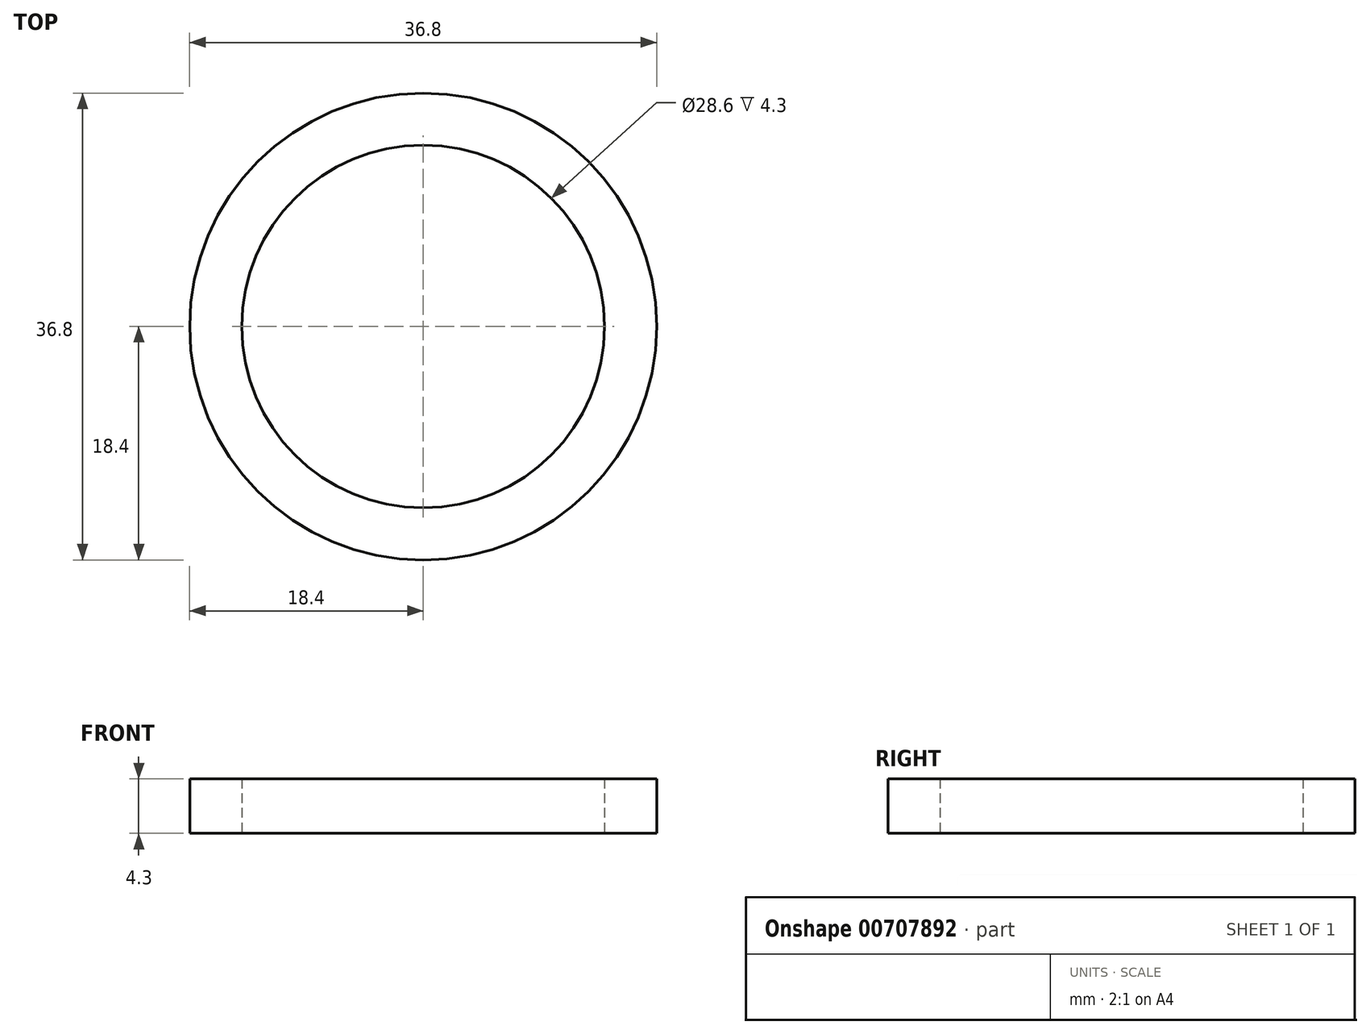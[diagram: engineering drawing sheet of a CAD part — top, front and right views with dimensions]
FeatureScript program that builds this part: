
annotation { "Feature Type Name" : "Feature", "Feature Type Description" : "" }
export const myFeature = defineFeature(function(context is Context, id is Id, definition is map)
    precondition{}
    {
        {
            var Q0;
            Q0=qCreatedBy(makeId("Top.planeOp"),FACE);
            var sketch = newSketch(context, id + "F0", { "sketchPlane" : qUnion([Q0])});
            skCircle(sketch, "E0", {"center": v(0, 0) * mm, "radius": 14.3 * mm});
            skCircle(sketch, "E1", {"center": v(0, 0) * mm, "radius": 18.4 * mm});
            skSolve(sketch);
        }
        {
            var Q0;
            Q0=makeQuery(id+"F0.imprint","IMPRINT",FACE,{"disambiguationData":[TD([[makeQuery(id+"F0.imprint","IMPRINT",EDGE,{"derivedFrom":sQuery(id+"F0.wireOp",EDGE,"E0")}),-1.0]])]});
            extrude(context, id + "F1", {"entities" : qUnion([Q0]), "depth" : 4.3 * mm, "offsetDistance" : 25 * mm});
        }
    });
